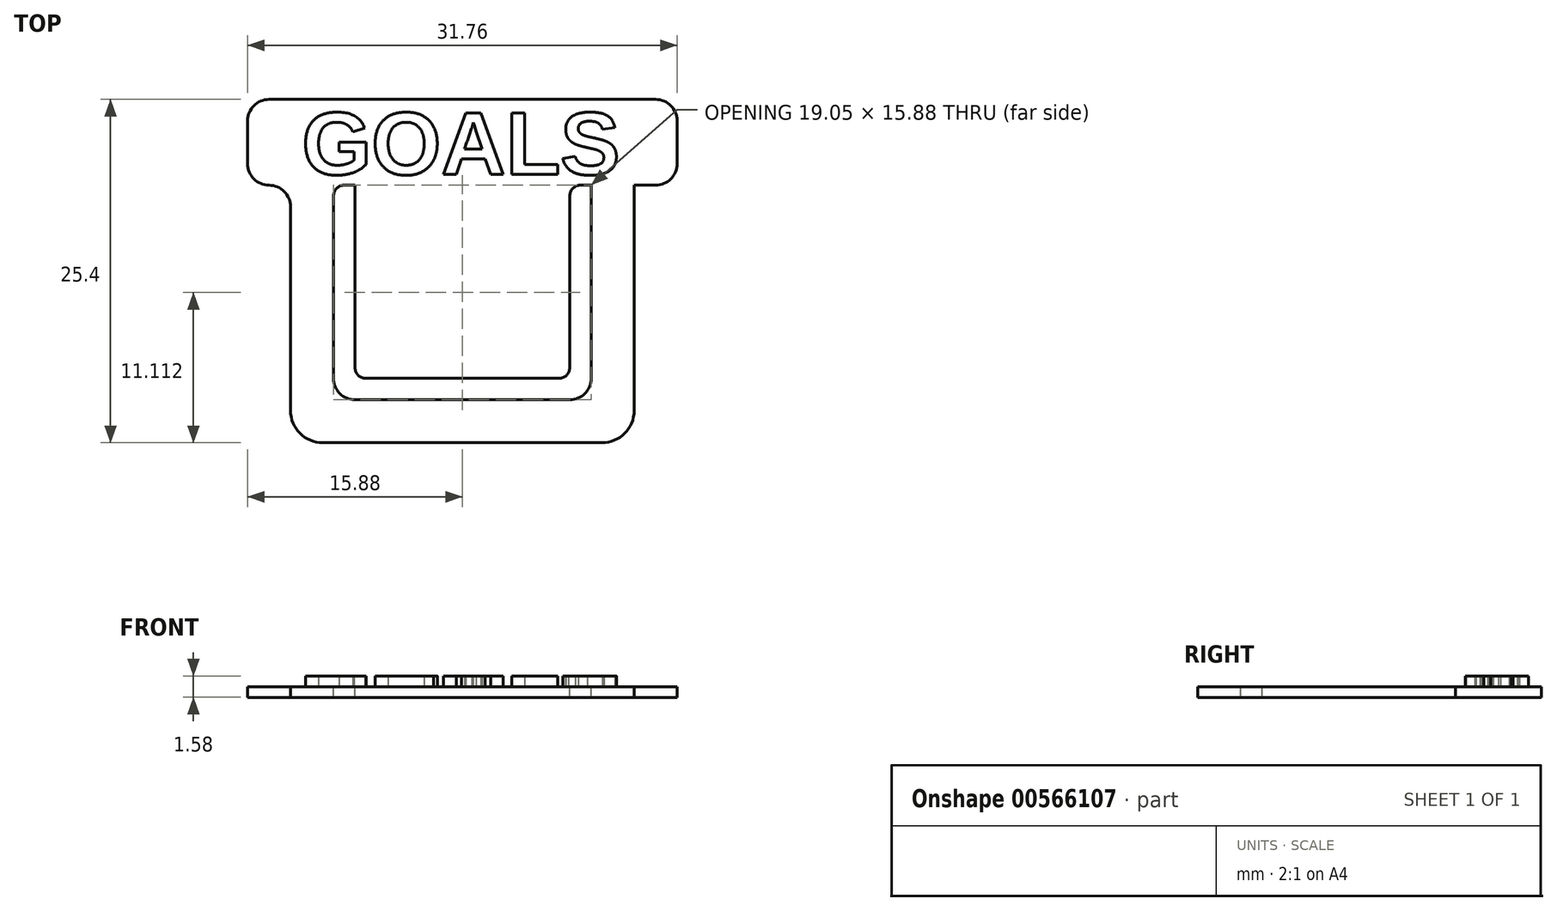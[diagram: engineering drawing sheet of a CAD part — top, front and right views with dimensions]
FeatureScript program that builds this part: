
annotation { "Feature Type Name" : "Feature", "Feature Type Description" : "" }
export const myFeature = defineFeature(function(context is Context, id is Id, definition is map)
    precondition{}
    {
        {
            var Q0;
            Q0=qCreatedBy(makeId("Front.planeOp"),FACE);
            var sketch = newSketch(context, id + "F0", { "sketchPlane" : qUnion([Q0])});
            skLineSegment(sketch, "E0.bottom", {"start": v(12.7, 9.53) * mm, "end": v(-12.7, 9.53) * mm});
            skLineSegment(sketch, "E0.top", {"start": v(12.7, -9.53) * mm, "end": v(-12.7, -9.53) * mm});
            skLineSegment(sketch, "E0.left", {"start": v(12.7, 9.53) * mm, "end": v(12.7, -9.53) * mm});
            skLineSegment(sketch, "E0.right", {"start": v(-12.7, 9.53) * mm, "end": v(-12.7, -9.53) * mm});
            skPoint(sketch, "E0.middle", {"position": v(0, 0) * mm});
            skSolve(sketch);
        }
        {
            var Q0;
            Q0=makeQuery(id+"F0.imprint","IMPRINT",FACE,{"disambiguationData":[TD([[makeQuery(id+"F0.imprint","IMPRINT",EDGE,{"derivedFrom":sQuery(id+"F0.wireOp",EDGE,"E0.bottom")}),1.0]])]});
            extrude(context, id + "F1", {"entities" : qUnion([Q0]), "depth" : 0.8 * mm, "offsetDistance" : 25.4 * mm});
        }
        {
            var Q0;
            Q0=makeQuery(id+"F1.opExtrude","SWEPT_EDGE",EDGE,{"disambiguationData":[OSD([sQuery(id+"F0.wireOp",EDGE,"E0.top"),sQuery(id+"F0.wireOp",EDGE,"E0.left")])]});
            var Q1;
            Q1=makeQuery(id+"F1.opExtrude","SWEPT_EDGE",EDGE,{"disambiguationData":[OSD([sQuery(id+"F0.wireOp",EDGE,"E0.top"),sQuery(id+"F0.wireOp",EDGE,"E0.right")])]});
            fillet(context, id + "F2", {"entities" : qUnion([Q0, Q1]), "radius" : 2.38 * mm, "tangentPropagation" : true, "allowEdgeOverflow" : false});
        }
        {
            var Q0;
            Q0=makeQuery(id+"F1.opExtrude","CAP_FACE",FACE,{"disambiguationData":[OSD([sQuery(id+"F0.wireOp",EDGE,"E0.bottom"),sQuery(id+"F0.wireOp",EDGE,"E0.top"),sQuery(id+"F0.wireOp",EDGE,"E0.left"),sQuery(id+"F0.wireOp",EDGE,"E0.right")])],"isStart":false});
            var sketch = newSketch(context, id + "F3", { "sketchPlane" : qUnion([Q0])});
            skLineSegment(sketch, "E1.bottom", {"start": v(9.52, 9.53) * mm, "end": v(-9.53, 9.53) * mm});
            skLineSegment(sketch, "E1.top", {"start": v(9.53, -6.35) * mm, "end": v(-9.53, -6.35) * mm});
            skLineSegment(sketch, "E1.left", {"start": v(9.52, 9.53) * mm, "end": v(9.53, -6.35) * mm});
            skLineSegment(sketch, "E1.right", {"start": v(-9.53, 9.53) * mm, "end": v(-9.52, -6.35) * mm});
            skPoint(sketch, "E1.middle", {"position": v(0, 0) * mm});
            skSolve(sketch);
        }
        {
            var Q0;
            Q0=makeQuery(id+"F3.imprint","IMPRINT",FACE,{"disambiguationData":[TD([[makeQuery(id+"F3.imprint","IMPRINT",EDGE,{"derivedFrom":sQuery(id+"F3.wireOp",EDGE,"E1.bottom")}),1.0]])]});
            extrude(context, id + "F4", {"entities" : qUnion([Q0]), "operationType" : NewBodyOperationType.REMOVE, "oppositeDirection" : true, "depth" : 4.93 * mm, "offsetDistance" : 25.4 * mm});
        }
        {
            var Q0;
            Q0=makeQuery(id+"F1.opExtrude","CAP_FACE",FACE,{"disambiguationData":[OSD([sQuery(id+"F0.wireOp",EDGE,"E0.bottom"),sQuery(id+"F0.wireOp",EDGE,"E0.top"),sQuery(id+"F0.wireOp",EDGE,"E0.left"),sQuery(id+"F0.wireOp",EDGE,"E0.right")])],"isStart":false});
            var sketch = newSketch(context, id + "F5", { "sketchPlane" : qUnion([Q0])});
            skLineSegment(sketch, "E2.bottom", {"start": v(-15.88, 9.53) * mm, "end": v(15.87, 9.53) * mm});
            skLineSegment(sketch, "E2.top", {"start": v(-15.88, 15.88) * mm, "end": v(15.87, 15.88) * mm});
            skLineSegment(sketch, "E2.left", {"start": v(-15.88, 9.53) * mm, "end": v(-15.88, 15.88) * mm});
            skLineSegment(sketch, "E2.right", {"start": v(15.87, 9.53) * mm, "end": v(15.87, 15.88) * mm});
            skSolve(sketch);
        }
        {
            var Q0;
            Q0=makeQuery(id+"F5.imprint","IMPRINT",FACE,{"disambiguationData":[TD([[makeQuery(id+"F5.imprint","IMPRINT",EDGE,{"derivedFrom":sQuery(id+"F5.wireOp",EDGE,"E2.top")}),-1.0]])]});
            extrude(context, id + "F6", {"entities" : qUnion([Q0]), "operationType" : NewBodyOperationType.ADD, "oppositeDirection" : true, "depth" : 0.8 * mm, "offsetDistance" : 25.4 * mm});
        }
        {
            var Q0;
            Q0=makeQuery(id+"F6.opExtrude","SWEPT_EDGE",EDGE,{"disambiguationData":[OSD([sQuery(id+"F5.wireOp",EDGE,"E2.top"),sQuery(id+"F5.wireOp",EDGE,"E2.left")])]});
            var Q1;
            Q1=makeQuery(id+"F6.opExtrude","SWEPT_EDGE",EDGE,{"disambiguationData":[OSD([sQuery(id+"F5.wireOp",EDGE,"E2.top"),sQuery(id+"F5.wireOp",EDGE,"E2.right")])]});
            var Q2;
            Q2=makeQuery(id+"F6.opExtrude","SWEPT_EDGE",EDGE,{"disambiguationData":[OSD([sQuery(id+"F5.wireOp",EDGE,"E2.bottom"),sQuery(id+"F5.wireOp",EDGE,"E2.right")])]});
            var Q3;
            Q3=makeQuery(id+"F1.opExtrude","SWEPT_EDGE",EDGE,{"disambiguationData":[OSD([sQuery(id+"F0.wireOp",EDGE,"E0.bottom"),sQuery(id+"F0.wireOp",EDGE,"E0.left")])]});
            var Q4;
            Q4=makeQuery(id+"F6.opExtrude","SWEPT_EDGE",EDGE,{"disambiguationData":[OSD([sQuery(id+"F5.wireOp",EDGE,"E2.bottom"),sQuery(id+"F5.wireOp",EDGE,"E2.left")])]});
            var Q5;
            Q5=makeQuery(id+"F1.opExtrude","SWEPT_EDGE",EDGE,{"disambiguationData":[OSD([sQuery(id+"F0.wireOp",EDGE,"E0.bottom"),sQuery(id+"F0.wireOp",EDGE,"E0.right")])]});
            fillet(context, id + "F7", {"entities" : qUnion([Q0, Q1, Q2, Q3, Q4, Q5]), "radius" : 1.59 * mm, "tangentPropagation" : true, "allowEdgeOverflow" : false});
        }
        {
            var Q0;
            Q0=makeQuery(id+"F4.boolean.opBoolean","COPY",EDGE,{"derivedFrom":makeQuery(id+"F4.opExtrude","SWEPT_EDGE",EDGE,{"disambiguationData":[OSD([sQuery(id+"F3.wireOp",EDGE,"E1.top"),sQuery(id+"F3.wireOp",EDGE,"E1.right")])]})});
            var Q1;
            Q1=makeQuery(id+"F4.boolean.opBoolean","COPY",EDGE,{"derivedFrom":makeQuery(id+"F4.opExtrude","SWEPT_EDGE",EDGE,{"disambiguationData":[OSD([sQuery(id+"F3.wireOp",EDGE,"E1.top"),sQuery(id+"F3.wireOp",EDGE,"E1.left")])]})});
            fillet(context, id + "F8", {"entities" : qUnion([Q0, Q1]), "radius" : 1.59 * mm, "tangentPropagation" : true, "allowEdgeOverflow" : false});
        }
        {
            var Q0;
            Q0=makeQuery(id+"F6.boolean.opBoolean","MERGE",FACE,{"derivedFrom":[makeQuery(id+"F1.opExtrude","CAP_FACE",FACE,{"disambiguationData":[OSD([sQuery(id+"F0.wireOp",EDGE,"E0.bottom"),sQuery(id+"F0.wireOp",EDGE,"E0.top"),sQuery(id+"F0.wireOp",EDGE,"E0.left"),sQuery(id+"F0.wireOp",EDGE,"E0.right")])],"isStart":false}),makeQuery(id+"F6.opExtrude","CAP_FACE",FACE,{"disambiguationData":[OSD([sQuery(id+"F5.wireOp",EDGE,"E2.bottom"),sQuery(id+"F5.wireOp",EDGE,"E2.top"),sQuery(id+"F5.wireOp",EDGE,"E2.left"),sQuery(id+"F5.wireOp",EDGE,"E2.right")])],"isStart":true})]});
            var sketch = newSketch(context, id + "F9", { "sketchPlane" : qUnion([Q0])});
            skLineSegment(sketch, "E3.bottom", {"start": v(-7.94, 9.53) * mm, "end": v(7.94, 9.53) * mm});
            skLineSegment(sketch, "E3.top", {"start": v(-7.94, -4.76) * mm, "end": v(7.94, -4.76) * mm});
            skLineSegment(sketch, "E3.left", {"start": v(-7.94, 9.53) * mm, "end": v(-7.94, -4.76) * mm});
            skLineSegment(sketch, "E3.right", {"start": v(7.94, 9.53) * mm, "end": v(7.94, -4.76) * mm});
            skSolve(sketch);
        }
        {
            var Q0;
            Q0=makeQuery(id+"F9.imprint","IMPRINT",FACE,{"disambiguationData":[TD([[makeQuery(id+"F9.imprint","IMPRINT",EDGE,{"derivedFrom":sQuery(id+"F9.wireOp",EDGE,"E3.bottom")}),1.0]])]});
            extrude(context, id + "F10", {"entities" : qUnion([Q0]), "operationType" : NewBodyOperationType.ADD, "oppositeDirection" : true, "depth" : 0.8 * mm, "offsetDistance" : 25.4 * mm});
        }
        {
            var Q0;
            Q0=makeQuery(id+"F10.boolean.opBoolean","MERGE",FACE,{"derivedFrom":[makeQuery(id+"F6.boolean.opBoolean","MERGE",FACE,{"derivedFrom":[makeQuery(id+"F1.opExtrude","CAP_FACE",FACE,{"disambiguationData":[OSD([sQuery(id+"F0.wireOp",EDGE,"E0.bottom"),sQuery(id+"F0.wireOp",EDGE,"E0.top"),sQuery(id+"F0.wireOp",EDGE,"E0.left"),sQuery(id+"F0.wireOp",EDGE,"E0.right")])],"isStart":false}),makeQuery(id+"F6.opExtrude","CAP_FACE",FACE,{"disambiguationData":[OSD([sQuery(id+"F5.wireOp",EDGE,"E2.bottom"),sQuery(id+"F5.wireOp",EDGE,"E2.top"),sQuery(id+"F5.wireOp",EDGE,"E2.left"),sQuery(id+"F5.wireOp",EDGE,"E2.right")])],"isStart":true})]}),makeQuery(id+"F10.opExtrude","CAP_FACE",FACE,{"disambiguationData":[OSD([sQuery(id+"F9.wireOp",EDGE,"E3.bottom"),sQuery(id+"F9.wireOp",EDGE,"E3.top"),sQuery(id+"F9.wireOp",EDGE,"E3.left"),sQuery(id+"F9.wireOp",EDGE,"E3.right")])],"isStart":true})]});
            var sketch = newSketch(context, id + "F11", { "sketchPlane" : qUnion([Q0])});
            skText(sketch, "E4", { "text": "GOALS\n", "fontName": "Arimo-Bold.ttf"});
            const initialGuessF11  = {"E4": [-0.01186, 0.01032, 1, 0, 0.00476]};
            skSetInitialGuess(sketch, initialGuessF11);
            skSolve(sketch);
        }
        {
            var Q0;
            Q0=makeQuery(id+"F11.imprint","IMPRINT",FACE,{"disambiguationData":[TD([[makeQuery(id+"F11.imprint","IMPRINT",EDGE,{"derivedFrom":sQuery(id+"F11.wireOp",EDGE,"E4.sketch_text.stroke-0")}),-1.0]])]});
            var Q1;
            Q1=makeQuery(id+"F11.imprint","IMPRINT",FACE,{"disambiguationData":[TD([[makeQuery(id+"F11.imprint","IMPRINT",EDGE,{"derivedFrom":sQuery(id+"F11.wireOp",EDGE,"E4.sketch_text.stroke-8")}),-1.0]])]});
            var Q2;
            Q2=makeQuery(id+"F11.imprint","IMPRINT",FACE,{"disambiguationData":[TD([[makeQuery(id+"F11.imprint","IMPRINT",EDGE,{"derivedFrom":sQuery(id+"F11.wireOp",EDGE,"E4.sketch_text.stroke-25")}),-1.0]])]});
            var Q3;
            Q3=makeQuery(id+"F11.imprint","IMPRINT",FACE,{"disambiguationData":[TD([[makeQuery(id+"F11.imprint","IMPRINT",EDGE,{"derivedFrom":sQuery(id+"F11.wireOp",EDGE,"E4.sketch_text.stroke-40")}),-1.0]])]});
            var Q4;
            Q4=makeQuery(id+"F11.imprint","IMPRINT",FACE,{"disambiguationData":[TD([[makeQuery(id+"F11.imprint","IMPRINT",EDGE,{"derivedFrom":sQuery(id+"F11.wireOp",EDGE,"E4.sketch_text.stroke-55")}),-1.0]])]});
            var Q5;
            Q5=makeQuery(id+"F11.imprint","IMPRINT",FACE,{"disambiguationData":[TD([[makeQuery(id+"F11.imprint","IMPRINT",EDGE,{"derivedFrom":sQuery(id+"F11.wireOp",EDGE,"E4.sketch_text.stroke-59")}),-1.0]])]});
            extrude(context, id + "F12", {"entities" : qUnion([Q0, Q1, Q2, Q3, Q4, Q5]), "operationType" : NewBodyOperationType.ADD, "depth" : 0.8 * mm, "offsetDistance" : 25.4 * mm});
        }
        {
            var Q0;
            Q0=makeQuery(id+"F10.opExtrude","SWEPT_EDGE",EDGE,{"disambiguationData":[OSD([sQuery(id+"F5.wireOp",EDGE,"E2.bottom"),sQuery(id+"F9.wireOp",EDGE,"E3.bottom"),sQuery(id+"F9.wireOp",EDGE,"E3.left")])]});
            var Q1;
            Q1=makeQuery(id+"F4.boolean.opBoolean","COPY",EDGE,{"derivedFrom":makeQuery(id+"F4.opExtrude","SWEPT_EDGE",EDGE,{"disambiguationData":[OSD([sQuery(id+"F0.wireOp",EDGE,"E0.bottom"),sQuery(id+"F3.wireOp",EDGE,"E1.bottom"),sQuery(id+"F3.wireOp",EDGE,"E1.right")])]})});
            var Q2;
            Q2=makeQuery(id+"F10.opExtrude","SWEPT_EDGE",EDGE,{"disambiguationData":[OSD([sQuery(id+"F5.wireOp",EDGE,"E2.bottom"),sQuery(id+"F9.wireOp",EDGE,"E3.bottom"),sQuery(id+"F9.wireOp",EDGE,"E3.right")])]});
            var Q3;
            Q3=makeQuery(id+"F4.boolean.opBoolean","COPY",EDGE,{"derivedFrom":makeQuery(id+"F4.opExtrude","SWEPT_EDGE",EDGE,{"disambiguationData":[OSD([sQuery(id+"F0.wireOp",EDGE,"E0.bottom"),sQuery(id+"F3.wireOp",EDGE,"E1.bottom"),sQuery(id+"F3.wireOp",EDGE,"E1.left")])]})});
            fillet(context, id + "F13", {"entities" : qUnion([Q0, Q1, Q2, Q3]), "radius" : 0.8 * mm, "tangentPropagation" : true, "allowEdgeOverflow" : false});
        }
        {
            var Q0;
            Q0=makeQuery(id+"F10.opExtrude","SWEPT_EDGE",EDGE,{"disambiguationData":[OSD([sQuery(id+"F9.wireOp",EDGE,"E3.top"),sQuery(id+"F9.wireOp",EDGE,"E3.left")])]});
            var Q1;
            Q1=makeQuery(id+"F10.opExtrude","SWEPT_EDGE",EDGE,{"disambiguationData":[OSD([sQuery(id+"F9.wireOp",EDGE,"E3.top"),sQuery(id+"F9.wireOp",EDGE,"E3.right")])]});
            fillet(context, id + "F14", {"entities" : qUnion([Q0, Q1]), "radius" : 0.8 * mm, "tangentPropagation" : true, "allowEdgeOverflow" : false});
        }
        {
            var Q0;
            Q0=makeQuery(id+"F1.opExtrude","SWEPT_BODY",BODY,{"disambiguationData":[OSD([sQuery(id+"F0.wireOp",EDGE,"E0.bottom"),sQuery(id+"F0.wireOp",EDGE,"E0.top"),sQuery(id+"F0.wireOp",EDGE,"E0.left"),sQuery(id+"F0.wireOp",EDGE,"E0.right")])]});
            var Q1;
            Q1=makeQuery(id+"F6.opExtrude","CAP_EDGE",EDGE,{"disambiguationData":[OSD([sQuery(id+"F5.wireOp",EDGE,"E2.top")])],"isStart":false});
            transform(context, id + "F15", {"entities" : qUnion([Q0]), "transformType" : TransformType.ROTATION, "transformAxis" : qUnion([Q1]), "angle" : 270 * degree, "makeCopy" : false});
        }
    });
